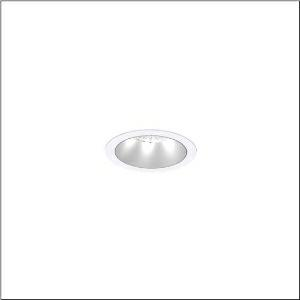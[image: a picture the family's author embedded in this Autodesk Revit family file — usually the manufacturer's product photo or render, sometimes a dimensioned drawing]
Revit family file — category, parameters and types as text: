
# Revit family: lunis_21_m_51db19mc91c
name_source: partatom
category: Lighting Fixtures
units: mm (PartAtom-declared; Revit-internal decimal feet)

## family parameters
Cut with Voids When Loaded = No
Host = Face
Light Source = No
Part Type = Normal
Room Calculation Point = No
Round Connector Dimension = Use Diameter
Shared = No

## types (1)
- --- (1 x LED, 3840 lm, 25.5 W, 6500K)
    Apparent Load = 26 VA
    CIE Flux Codes = 93 99 100 100 100
    Color Rendering = 80
    Color Temperature = 6500K
    Default Elevation = 1800 mm
    Description = Lunis 21,  M, downlight, light control with lens, of PMMA, anti glare with reflector, of PC, matt, light emission: direct distribution, LED rated luminous flux: 1.770lm, light colour: 830/840/865, with terminal, 3-pole, mains connection: 220..240V, AC/DC, 0/50..60Hz, housing, round, of diecast aluminium, traffic white (RAL 9016), diameter: 115mm, clamping range: 1..40mm, protection rating (complete): IP20, protection rating (on room side): IP54, insulation class (complete): insulation class II (safety insulation), certification: CE, impact resistance: IK03, packaging unit: 1 piece
    Height = 0 mm  [stored 0 ft]
    Lamp = 1 x LED
    Lamp Light Flux = 3840 lm
    Lamp Power = 25.5 W
    Lamp count = 1
    Length = 115 mm
    Luminous efficacy = 151 lm/W
    Manufacturer = Siteco
    ModVariant = No
    Model = 51DB19MC91C
    Mounting Place = Ceiling
    Mounting Type = Recessed
    Number of Poles = 1
    OnlyDefault = Yes
    Power Factor = 1
    Product Name = Lunis 21 M
    Product group = downlight
    ProductGroupID = 401
    Protection Class = Protection class II
    Protection Degree = IP 20
    RLX_Detail_Level = 1
    RLX_Emergency_Light_Flux = 0 lm
    RLX_Emergency_Type = 0
    RLX_Emergency_Type_DB = No
    RlxData = <blob elided: 15009 chars, md5=3e309205>
    Socket = socket
    Standby Power = 0 W
    System Light Flux = 3840 lm
    System Power = 26 W
    Type Comments = individual setting: colour temperature 6500K, luminous flux: 100 % | (ON | ON | OFF | OFF) | 700 mA
    Type Image = l_1290856.jpg
    URL = http://relux.com
    VarID = @adj_039099
    Voltage = 0 V
    Weight = 0.00 kg
    Width = 0 mm  [stored 0 ft]

note: [stored X ft] marks values corroborated as IEEE doubles in the binary element streams (Revit-internal decimal feet)

## geometry (parser evidence)
native form markers: Sweep x11
no freeform markers — native parametric forms only
